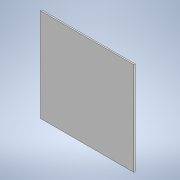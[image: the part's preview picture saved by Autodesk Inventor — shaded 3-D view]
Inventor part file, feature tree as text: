
AUTODESK INVENTOR PART (.ipt)
format: ipt  version: 2020.1 (Build 241239000, 239)  size: 189,440 bytes
history: native  units: in
note: dims shown in document units (in); Inventor stores cm internally (conversion verified against a paired STEP export)
features: extrude x8, sketch x8, fillet x1
ambient origin geometry x8: Origin, YZ Plane, XZ Plane, XY Plane, X Axis, Y Axis, Z Axis, Center Point
bodies: Solid1 (feature_tree)
feature tree (17):
  extrude  "Extrusion1"  Depth=2.5591in
  extrude  "Extrusion2"  Depth=0.0394in TaperAngle=0.0deg
  sketch  "Sketch3"  dims[d18=0.0394in d19=0.0in d23=1.811in]
  extrude  "Extrusion5"  Depth=0.0394in
  extrude  "Extrusion6"  Depth=0.1181in TaperAngle=0.0deg
  extrude  "Extrusion7"  Depth=0.0394in TaperAngle=0.0deg
  extrude  "Extrusion8"  Depth=0.3937in
  extrude  "Extrusion9"  Depth=0.0394in TaperAngle=0.0deg
  extrude  "Extrusion11"  Depth=0.2559in
  fillet  "Fillet1"  Radius=0.0197in
  sketch  "Sketch1"  dims[d0=2.5591in d1=2.5591in]
  sketch  "Sketch2"  dims[d2=0.0906in d3=0.0in d5=0.0394in d6=0.0in]
  sketch  "Sketch6"  dims[d24=0.1181in d25=0.0in d29=0.1181in d30=0.0in]
  sketch  "Sketch7"  dims[d32=0.0394in d33=0.0394in d34=0.0in]
  sketch  "Sketch8"  dims[d35=0.0787in d36=0.3937in]
  sketch  "Sketch9"  dims[d37=0.4724in d39=0.0394in d40=0.0in]
  sketch  "Sketch12"  dims[d45=0.1181in d46=0.0in d47=0.2559in d43=0.0197in d44=0.0344in]
